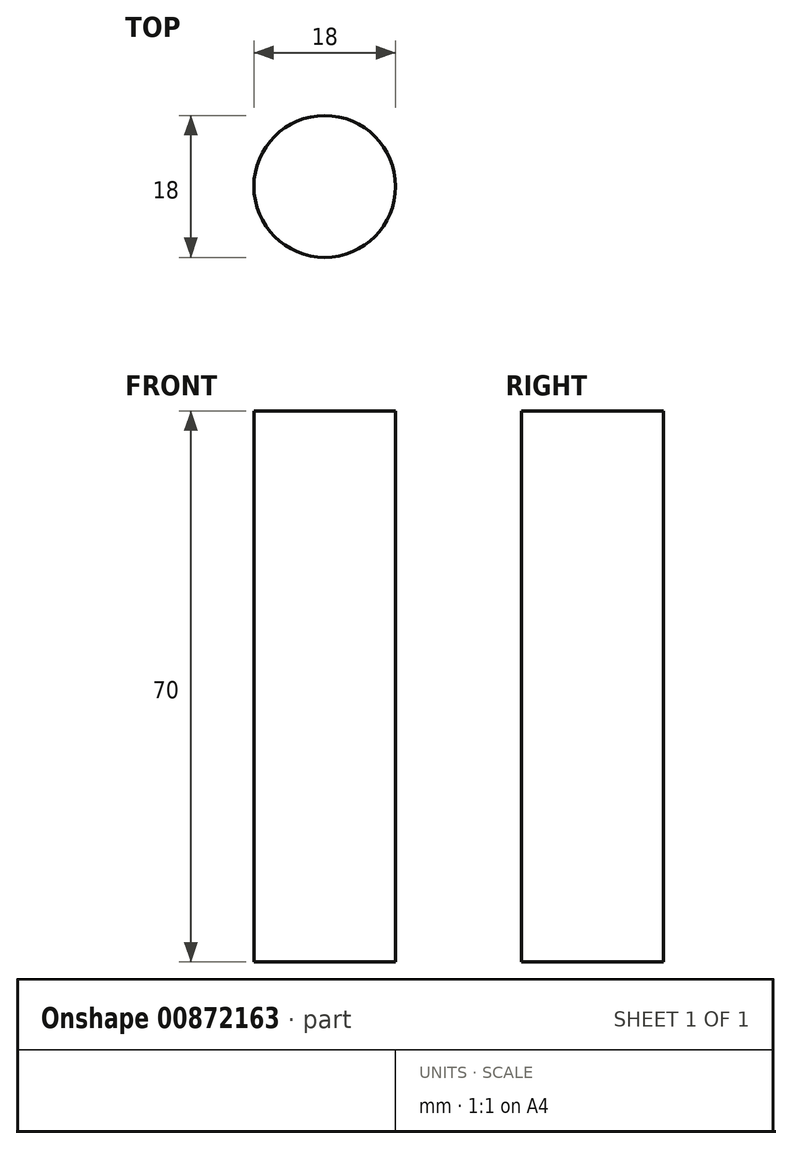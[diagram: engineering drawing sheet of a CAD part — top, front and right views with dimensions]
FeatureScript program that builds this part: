
annotation { "Feature Type Name" : "Feature", "Feature Type Description" : "" }
export const myFeature = defineFeature(function(context is Context, id is Id, definition is map)
    precondition{}
    {
        {
            var Q0;
            Q0=qCreatedBy(makeId("Top.planeOp"),FACE);
            var sketch = newSketch(context, id + "F0", { "sketchPlane" : qUnion([Q0])});
            skLineSegment(sketch, "E0", {"start": v(0, 0) * mm, "end": v(0, 16.51) * mm});
            skCircle(sketch, "E1", {"center": v(0, 16.51) * mm, "radius": 9 * mm});
            skSolve(sketch);
        }
        {
            var Q0;
            Q0=makeQuery(id+"F0.imprint","IMPRINT",FACE,{"disambiguationData":[TD([[makeQuery(id+"F0.imprint","IMPRINT",EDGE,{"derivedFrom":sQuery(id+"F0.wireOp",EDGE,"E1")}),1.0]])]});
            extrude(context, id + "F1", {"entities" : qUnion([Q0]), "depth" : 70 * mm, "offsetDistance" : 25.4 * mm});
        }
        {
            var Q0;
            Q0=qCreatedBy(makeId("Front.planeOp"),FACE);
            var sketch = newSketch(context, id + "F2", { "sketchPlane" : qUnion([Q0])});
            skLineSegment(sketch, "E2", {"start": v(0, 106.62) * mm, "end": v(0, -49.3) * mm});
            skSolve(sketch);
        }
    });
